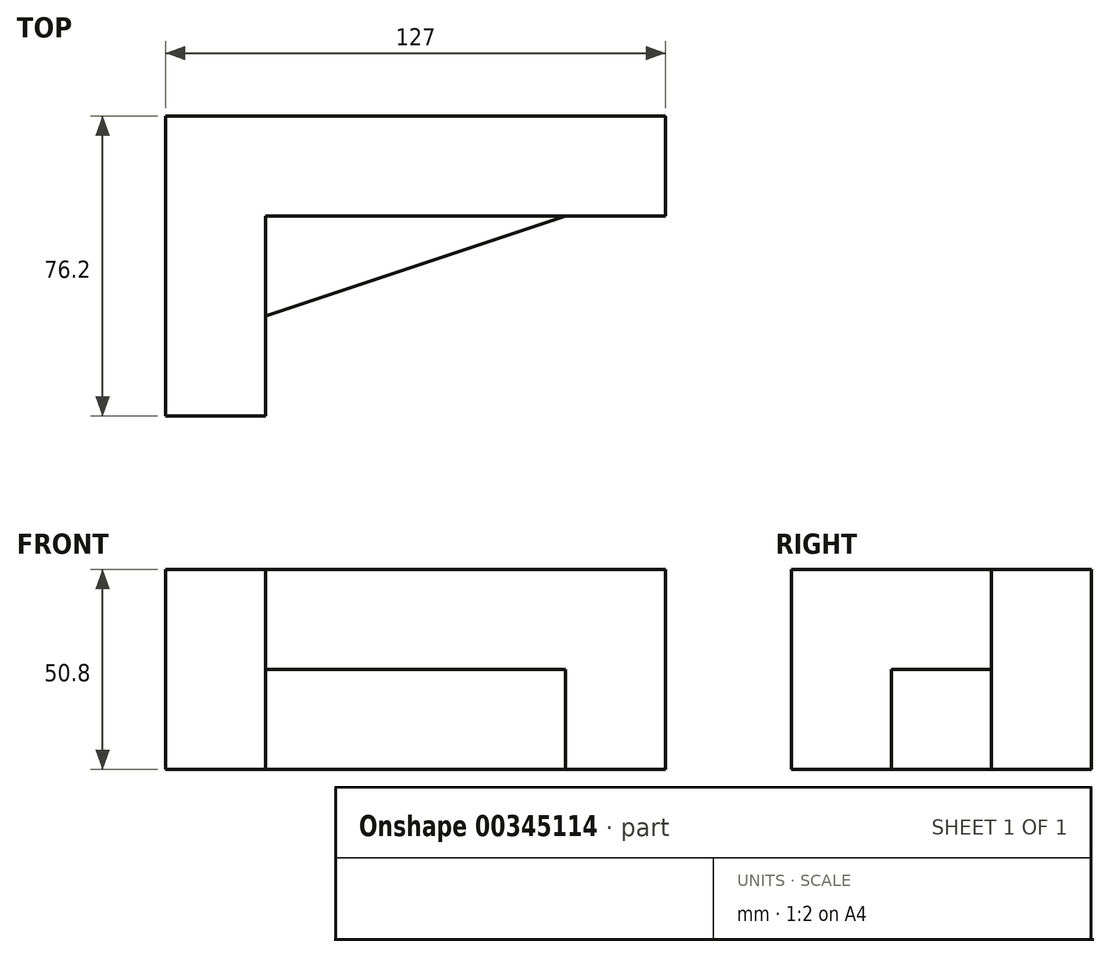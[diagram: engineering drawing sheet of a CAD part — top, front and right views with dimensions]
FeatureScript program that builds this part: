
annotation { "Feature Type Name" : "Feature", "Feature Type Description" : "" }
export const myFeature = defineFeature(function(context is Context, id is Id, definition is map)
    precondition{}
    {
        {
            var Q0;
            Q0=qCreatedBy(makeId("Top.planeOp"),FACE);
            var sketch = newSketch(context, id + "F0", { "sketchPlane" : qUnion([Q0])});
            skLineSegment(sketch, "E0", {"start": v(0, 0) * mm, "end": v(0, 76.2) * mm});
            skLineSegment(sketch, "E1", {"start": v(0, 76.2) * mm, "end": v(127, 76.2) * mm});
            skLineSegment(sketch, "E2", {"start": v(127, 76.2) * mm, "end": v(127, 50.8) * mm});
            skLineSegment(sketch, "E3", {"start": v(127, 50.8) * mm, "end": v(101.6, 50.8) * mm});
            skLineSegment(sketch, "E4", {"start": v(101.6, 50.8) * mm, "end": v(25.4, 25.4) * mm});
            skLineSegment(sketch, "E5", {"start": v(25.4, 25.4) * mm, "end": v(25.4, 0) * mm});
            skLineSegment(sketch, "E6", {"start": v(25.4, 0) * mm, "end": v(0, 0) * mm});
            skSolve(sketch);
        }
        {
            var Q0;
            Q0 = qSketchRegion(id + "F0", true);
            extrude(context, id + "F1", {"entities" : qUnion([Q0]), "depth" : 50.8 * mm});
        }
        {
            var Q0;
            Q0=makeQuery(id+"F1.opExtrude","CAP_FACE",FACE,{"disambiguationData":[OSD([sQuery(id+"F0.wireOp",EDGE,"E0"),sQuery(id+"F0.wireOp",EDGE,"E1"),sQuery(id+"F0.wireOp",EDGE,"E2"),sQuery(id+"F0.wireOp",EDGE,"E3"),sQuery(id+"F0.wireOp",EDGE,"E4"),sQuery(id+"F0.wireOp",EDGE,"E5"),sQuery(id+"F0.wireOp",EDGE,"E6")])],"isStart":false});
            var sketch = newSketch(context, id + "F2", { "sketchPlane" : qUnion([Q0])});
            skLineSegment(sketch, "E7", {"start": v(101.6, 50.8) * mm, "end": v(25.37, 50.8) * mm});
            skLineSegment(sketch, "E8", {"start": v(25.37, 50.8) * mm, "end": v(25.4, 25.4) * mm});
            skLineSegment(sketch, "E9", {"start": v(25.4, 25.4) * mm, "end": v(101.6, 50.8) * mm});
            skSolve(sketch);
        }
        {
            var Q0;
            Q0 = qSketchRegion(id + "F2", true);
            extrude(context, id + "F3", {"entities" : qUnion([Q0]), "operationType" : NewBodyOperationType.REMOVE, "oppositeDirection" : true, "depth" : 25.4 * mm});
        }
    });
